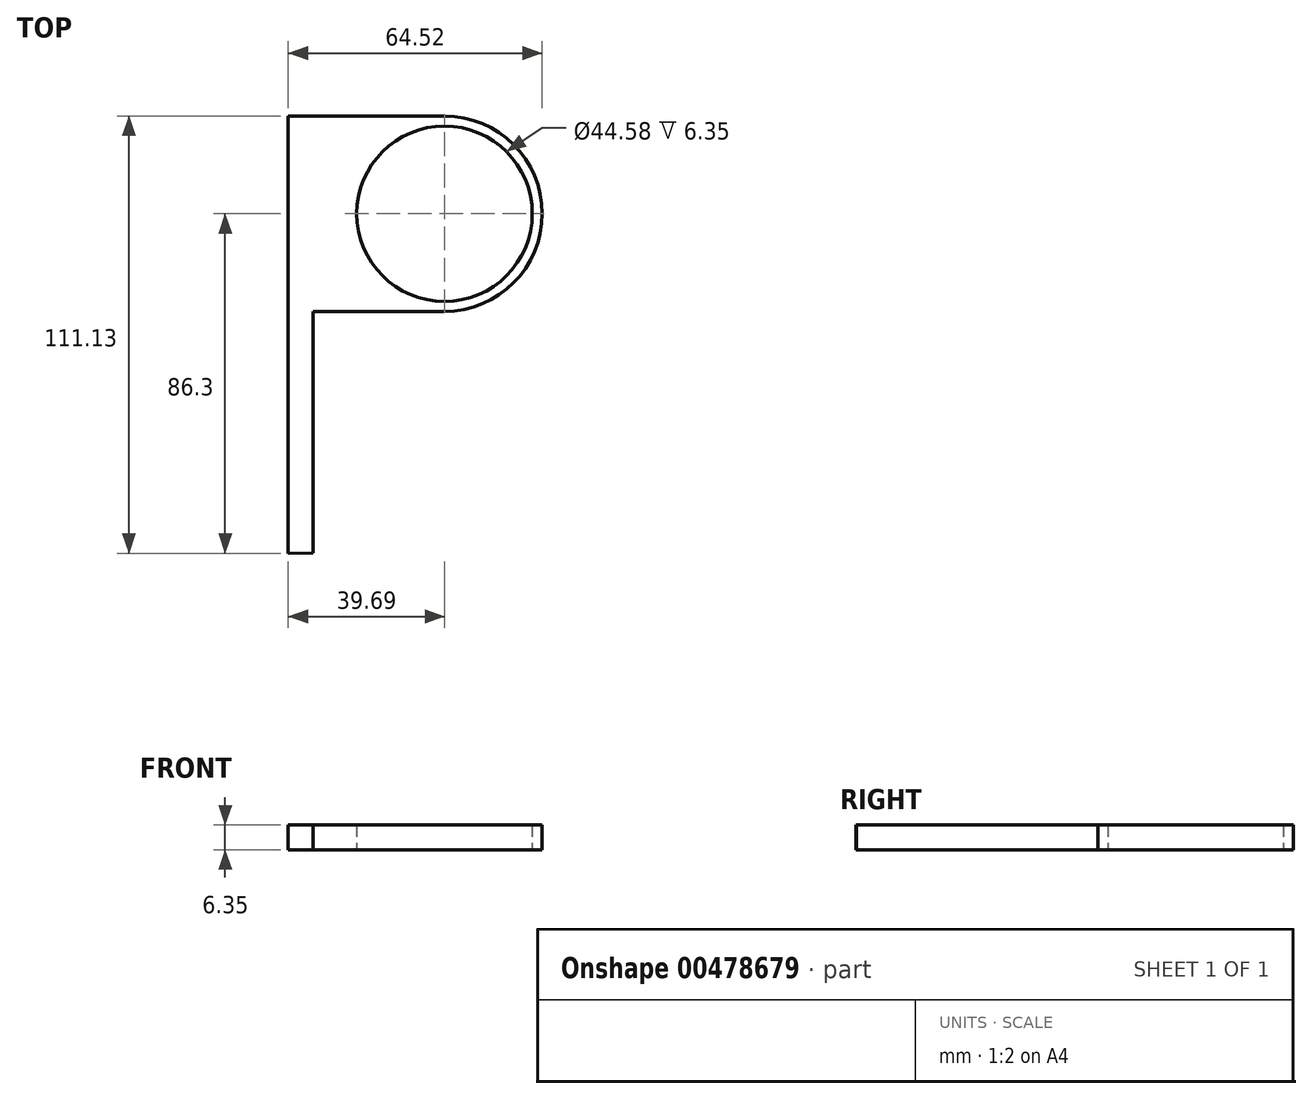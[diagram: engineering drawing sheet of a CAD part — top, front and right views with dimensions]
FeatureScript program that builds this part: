
annotation { "Feature Type Name" : "Feature", "Feature Type Description" : "" }
export const myFeature = defineFeature(function(context is Context, id is Id, definition is map)
    precondition{}
    {
        {
            var Q0;
            Q0=qCreatedBy(makeId("Top.planeOp"),FACE);
            var sketch = newSketch(context, id + "F0", { "sketchPlane" : qUnion([Q0])});
            skCircle(sketch, "E0", {"center": v(0, 0) * mm, "radius": 22.29 * mm});
            skArc(sketch, "E1", {"start": v(0, -24.83) * mm, "mid": v(24.83, 0) * mm, "end": v(0, 24.83) * mm});
            skLineSegment(sketch, "E2", {"start": v(-39.69, 24.83) * mm, "end": v(-39.69, -86.3) * mm});
            skLineSegment(sketch, "E3", {"start": v(0, 24.83) * mm, "end": v(-39.69, 24.83) * mm});
            skLineSegment(sketch, "E4", {"start": v(0, -24.83) * mm, "end": v(-33.34, -24.83) * mm});
            skLineSegment(sketch, "E5", {"start": v(-33.34, -24.83) * mm, "end": v(-33.34, -86.23) * mm});
            skLineSegment(sketch, "E6", {"start": v(-33.34, -86.23) * mm, "end": v(-39.69, -86.3) * mm});
            skSolve(sketch);
        }
        {
            var Q0;
            Q0 = qSketchRegion(id + "F0", true);
            extrude(context, id + "F1", {"entities" : qUnion([Q0]), "depth" : 6.35 * mm, "offsetDistance" : 25.4 * mm});
        }
    });
